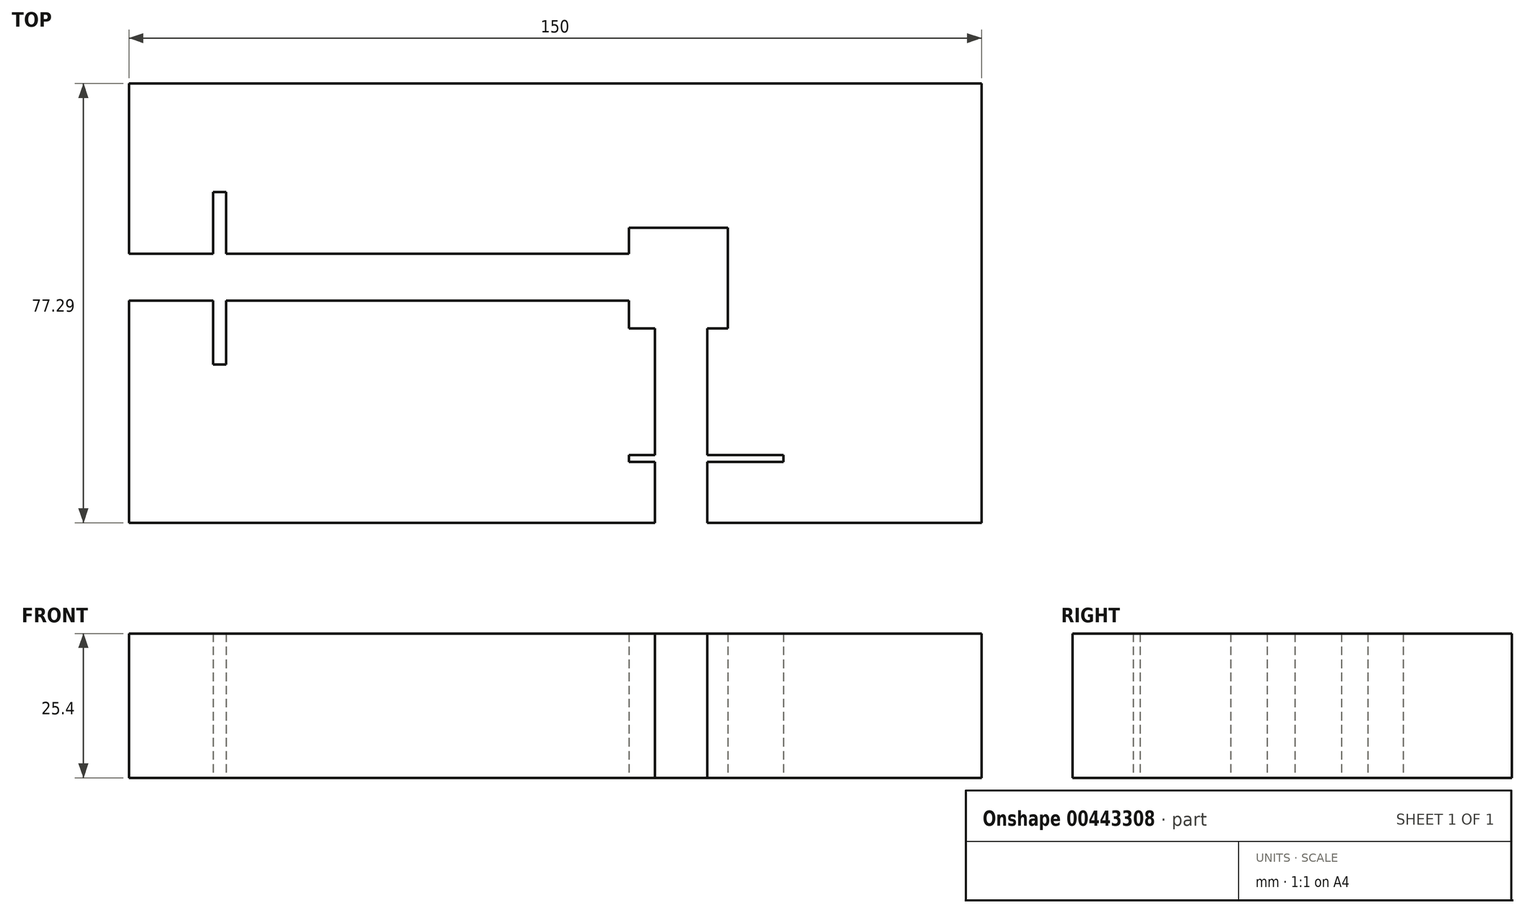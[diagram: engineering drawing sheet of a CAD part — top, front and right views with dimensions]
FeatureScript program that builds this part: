
annotation { "Feature Type Name" : "Feature", "Feature Type Description" : "" }
export const myFeature = defineFeature(function(context is Context, id is Id, definition is map)
    precondition{}
    {
        {
            var Q0;
            Q0=qCreatedBy(makeId("Top.planeOp"),FACE);
            var sketch = newSketch(context, id + "F0", { "sketchPlane" : qUnion([Q0])});
            skLineSegment(sketch, "E0.bottom", {"start": v(-68.63, 35) * mm, "end": v(81.37, 35) * mm});
            skLineSegment(sketch, "E0.top", {"start": v(-68.63, -42.29) * mm, "end": v(81.37, -42.29) * mm});
            skLineSegment(sketch, "E0.left", {"start": v(-68.63, 35) * mm, "end": v(-68.63, -42.29) * mm});
            skLineSegment(sketch, "E0.right", {"start": v(81.37, 35) * mm, "end": v(81.37, -42.29) * mm});
            skLineSegment(sketch, "E1.bottom", {"start": v(-68.63, 5.06) * mm, "end": v(19.36, 5.06) * mm});
            skLineSegment(sketch, "E1.top", {"start": v(-68.63, -3.18) * mm, "end": v(19.36, -3.18) * mm});
            skLineSegment(sketch, "E1.left", {"start": v(-68.63, 5.06) * mm, "end": v(-68.63, -3.18) * mm});
            skLineSegment(sketch, "E1.right", {"start": v(19.36, 5.06) * mm, "end": v(19.36, -3.18) * mm});
            skLineSegment(sketch, "E2.bottom", {"start": v(19.36, 9.65) * mm, "end": v(36.77, 9.65) * mm});
            skLineSegment(sketch, "E2.top", {"start": v(19.36, -8.07) * mm, "end": v(36.77, -8.07) * mm});
            skLineSegment(sketch, "E2.left", {"start": v(19.36, 9.65) * mm, "end": v(19.36, -8.07) * mm});
            skLineSegment(sketch, "E2.right", {"start": v(36.77, 9.65) * mm, "end": v(36.77, -8.07) * mm});
            skLineSegment(sketch, "E3.bottom", {"start": v(23.94, -8.07) * mm, "end": v(33.1, -8.07) * mm});
            skLineSegment(sketch, "E3.top", {"start": v(23.94, -42.29) * mm, "end": v(33.1, -42.29) * mm});
            skLineSegment(sketch, "E3.left", {"start": v(23.94, -8.07) * mm, "end": v(23.94, -42.29) * mm});
            skLineSegment(sketch, "E3.right", {"start": v(33.1, -8.07) * mm, "end": v(33.1, -42.29) * mm});
            skLineSegment(sketch, "E4.bottom", {"start": v(19.36, -30.37) * mm, "end": v(46.55, -30.37) * mm});
            skLineSegment(sketch, "E4.top", {"start": v(19.36, -31.6) * mm, "end": v(46.55, -31.6) * mm});
            skLineSegment(sketch, "E4.left", {"start": v(19.36, -30.37) * mm, "end": v(19.36, -31.6) * mm});
            skLineSegment(sketch, "E4.right", {"start": v(46.55, -30.37) * mm, "end": v(46.55, -31.6) * mm});
            skLineSegment(sketch, "E5.bottom", {"start": v(-53.81, 15.88) * mm, "end": v(-51.5, 15.88) * mm});
            skLineSegment(sketch, "E5.top", {"start": v(-53.81, -14.43) * mm, "end": v(-51.5, -14.43) * mm});
            skLineSegment(sketch, "E5.left", {"start": v(-53.81, 15.88) * mm, "end": v(-53.81, -14.43) * mm});
            skLineSegment(sketch, "E5.right", {"start": v(-51.5, 15.88) * mm, "end": v(-51.5, -14.43) * mm});
            skSolve(sketch);
        }
        {
            var Q0;
            {var subQ0=sQuery(id+"F0.wireOp",EDGE,"E1.left");Q0=makeQuery(id+"F0.imprint","IMPRINT",FACE,{"disambiguationData":[TD([[makeQuery(id+"F0.imprint","IMPRINT",EDGE,{"derivedFrom":subQ0}),1.0]])]});}
            var Q1;
            {var subQ0=sQuery(id+"F0.wireOp",EDGE,"E3.top");Q1=makeQuery(id+"F0.imprint","IMPRINT",FACE,{"disambiguationData":[TD([[makeQuery(id+"F0.imprint","IMPRINT",EDGE,{"derivedFrom":subQ0}),1.0]])]});}
            var Q2;
            {var subQ0=sQuery(id+"F0.wireOp",EDGE,"E4.left");Q2=makeQuery(id+"F0.imprint","IMPRINT",FACE,{"disambiguationData":[TD([[makeQuery(id+"F0.imprint","IMPRINT",EDGE,{"derivedFrom":subQ0}),-1.0]])]});}
            var Q3;
            {var subQ14=sQuery(id+"F0.wireOp",EDGE,"E0.bottom");Q3=makeQuery(id+"F0.imprint","IMPRINT",FACE,{"disambiguationData":[TD([[makeQuery(id+"F0.imprint","IMPRINT",EDGE,{"derivedFrom":subQ14}),-1.0]])]});}
            extrude(context, id + "F1", {"entities" : qUnion([Q0, Q1, Q2, Q3]), "depth" : 25.4 * mm});
        }
    });
